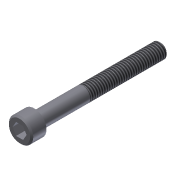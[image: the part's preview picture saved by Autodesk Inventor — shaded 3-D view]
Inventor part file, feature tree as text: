
AUTODESK INVENTOR PART (.ipt)
format: ipt  version: 2011 SP1 (Build 150282100, 282)  size: 99,328 bytes
history: native  units: in
note: dims shown in document units (in); Inventor stores cm internally (conversion verified against a paired STEP export)
features: extrude x3, sketch x3, chamfer x2, thread x1
ambient origin geometry x8: Origin, YZ Plane, XZ Plane, XY Plane, X Axis, Y Axis, Z Axis, Center Point
bodies: Solid1 (feature_tree)
feature tree (9):
  extrude  "Extrusion1"  Depth=0.19in TaperAngle=0.0deg
  extrude  "Extrusion2"  Depth=1.625in TaperAngle=0.0deg
  extrude  "Extrusion3"  Depth=0.125in TaperAngle=0.0deg
  thread  "Thread1"  [1 undecoded]
  chamfer  "Chamfer1"  Distance=0.02in Angle=45.0deg
  chamfer  "Chamfer2"  Distance=0.02in Angle=45.0deg
  sketch  "Sketch1"  dims[d0=0.312in d1=0.19in d2=0.0in]
  sketch  "Sketch2"  dims[d3=0.19in d4=1.625in d5=0.0in]
  sketch  "Sketch3"  dims[d6=0.1562in d7=0.125in d8=0.0in d9=1.0in d10=0.0in d11=0.02in d12=0.125in d13=45.0deg d14=0.02in d15=0.125in d16=45.0deg]
note: 1 required parameter value undecoded (feature->parameter linkage not recoverable at this tier; creation-order binding heuristic only, values carry confidence <= 0.55)
